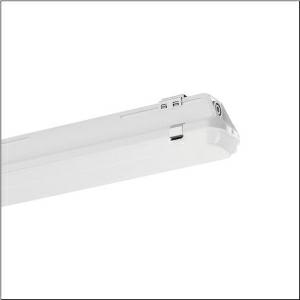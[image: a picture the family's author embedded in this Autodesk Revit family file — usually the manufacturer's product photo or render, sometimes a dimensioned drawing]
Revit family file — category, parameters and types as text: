
# Revit family: monsun_r__21_emergency_51fb207p437c3g_e70d
name_source: partatom
category: Lighting Fixtures
units: mm (PartAtom-declared; Revit-internal decimal feet)

## family parameters
Cut with Voids When Loaded = No
Host = Face
Light Source = No
Part Type = Normal
Room Calculation Point = No
Round Connector Dimension = Use Diameter
Shared = No

## types (1)
- --- (1 x LED, 820 lm, 7.1 W, 4000K)
    Apparent Load = 7 VA
    CIE Flux Codes = 45 75 93 94 100
    Color Rendering = 80
    Color Temperature = 4000K
    Default Elevation = 1800 mm
    Description = Monsun® 21 emergency, damp-proof luminaire, chain hanger, primary optical cover: enclosure, of PC, light emission: direct distribution, primary light characteristic: symmetric, installation type: suspended mounting, surface-mounted, horizontal mounting, vertical mounting, LED, rated luminous flux: 3.620lm, luminous efficacy: 157lm/W, light colour: 840, colour temperature: 4000K, control gear: ON/OFF, with terminal, 4-pole, max. 2.5mm², mains connection: 220..240V, AC, 50/60Hz, rated input power: 27W, control gear: single battery element, battery: LiFePO4, 9Ah, housing, of glass-fibre reinforced polyester, uncoated, bright grey, incl. chain hanger, length: 1.590mm, width: 90mm, height: 88mm, clip for enclosure, of stainless steel (V2A), ceiling mounting element, of stainless steel (V2A), chain hanger, of stainless steel (V2A), protection rating (complete): IP66, insulation class (complete): insulation class I (protective earthing), certification: CE, UKCA, protection symbol: D, impact resistance: IK08, permissible operating ambient temperature: +5..+25°C, standard: EN 50419, EN 60598-2-1, EN 60598-2-22, corresponds to IFS (International Featured Standards) requirements for safety and quality in the food industry, for indoor or canopied outdoor use, no direct snow, no direct sun, no direct rain, LABS conformity tested according to VDMA 24364:2018-05, contact your sales advisor before using the luminaires in applications with unclear chemical exposure, large temperature fluctuations or condensation-forming humidity, packaging unit: 1 piece
    Height = 89 mm
    Lamp = 1 x LED
    Lamp Light Flux = 820 lm
    Lamp Power = 7.1 W
    Lamp count = 1
    Length = 1590 mm
    Luminous efficacy = 115 lm/W
    Manufacturer = Siteco
    ModVariant = No
    Model = 51FB207P437C3G
    Mounting Place = Ceiling
    Mounting Type = Surface mounted
    Number of Poles = 1
    OnlyDefault = Yes
    Power Factor = 1
    Product Name = Monsun® 21 emergency
    Product group = damp-proof luminaire
    ProductGroupID = 301
    Protection Class = Protection class I
    Protection Degree = IP 66
    RLX_Detail_Level = 1
    RLX_Emergency_Light_Flux = 0 lm
    RLX_Emergency_Type = 0
    RLX_Emergency_Type_DB = No
    RlxData = <blob elided: 88801 chars, md5=83d6a3f0>
    Socket = socket
    Standby Power = 0 W
    System Light Flux = 820 lm
    System Power = 7 W
    Type Comments = : emergency light operation: 3 h
    Type Image = l_1319656.jpg
    URL = http://relux.com
    VarID = @adj_062715
    Voltage = 0 V
    Weight = 0.00 kg
    Width = 90 mm

## geometry (parser evidence)
native form markers: Blend x4, Sweep x13
no freeform markers — native parametric forms only
